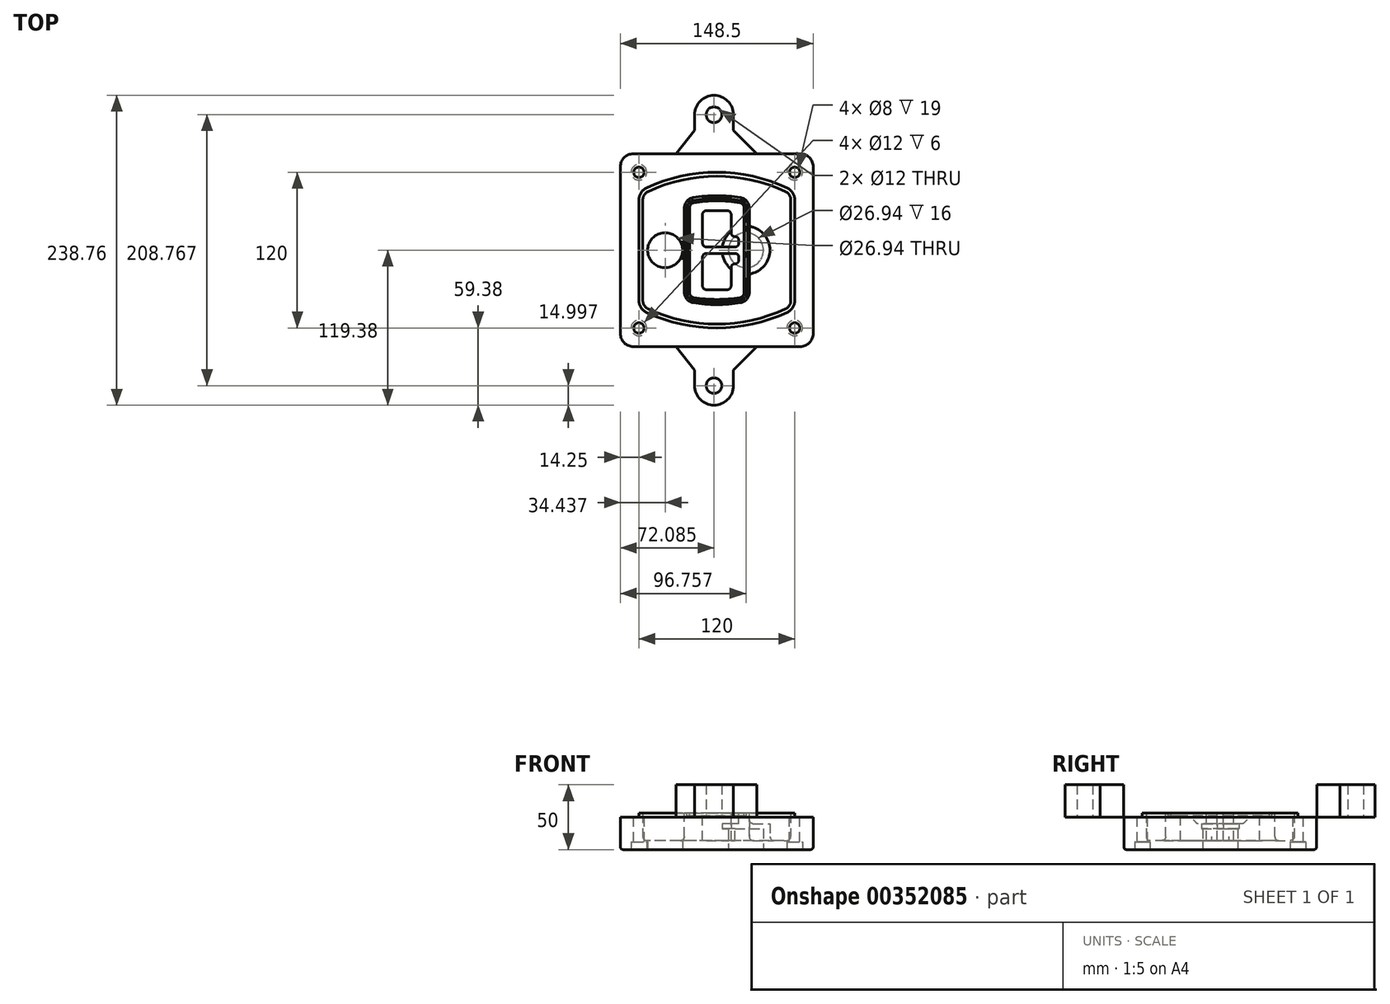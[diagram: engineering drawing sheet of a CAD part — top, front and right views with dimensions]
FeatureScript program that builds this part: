
annotation { "Feature Type Name" : "Feature", "Feature Type Description" : "" }
export const myFeature = defineFeature(function(context is Context, id is Id, definition is map)
    precondition{}
    {
        {
            var Q0;
            Q0=qCreatedBy(makeId("Top.planeOp"),FACE);
            var sketch = newSketch(context, id + "F0", { "sketchPlane" : qUnion([Q0])});
            skPoint(sketch, "E0.rect.middle", {"position": v(0, 0) * mm});
            skLineSegment(sketch, "E1.bottom", {"start": v(-64.25, -74.25) * mm, "end": v(64.25, -74.25) * mm});
            skLineSegment(sketch, "E1.top", {"start": v(-64.25, 74.25) * mm, "end": v(64.25, 74.25) * mm});
            skLineSegment(sketch, "E1.left", {"start": v(-74.25, -64.25) * mm, "end": v(-74.25, 64.25) * mm});
            skLineSegment(sketch, "E1.right", {"start": v(74.25, -64.25) * mm, "end": v(74.25, 64.25) * mm});
            skLineSegment(sketch, "E2", {"start": v(-74.25, 74.25) * mm, "end": v(74.25, -74.25) * mm, "construction": true});
            skLineSegment(sketch, "E3", {"start": v(74.25, 74.25) * mm, "end": v(-74.25, -74.25) * mm, "construction": true});
            skCircle(sketch, "E4", {"center": v(-60, 60) * mm, "radius": 4 * mm});
            skCircle(sketch, "E5", {"center": v(60, 60) * mm, "radius": 4 * mm});
            skCircle(sketch, "E6", {"center": v(60, -60) * mm, "radius": 4 * mm});
            skCircle(sketch, "E7", {"center": v(-60, -60) * mm, "radius": 4 * mm});
            skLineSegment(sketch, "E8", {"start": v(-60, 60) * mm, "end": v(60, 60) * mm, "construction": true});
            skLineSegment(sketch, "E9", {"start": v(60, 60) * mm, "end": v(60, -60) * mm, "construction": true});
            skLineSegment(sketch, "E10", {"start": v(60, -60) * mm, "end": v(-60, -60) * mm, "construction": true});
            skLineSegment(sketch, "E11", {"start": v(-60, -60) * mm, "end": v(-60, 60) * mm, "construction": true});
            skLineSegment(sketch, "E12", {"start": v(-60, 38.83) * mm, "end": v(-60, -38.83) * mm});
            skLineSegment(sketch, "E13", {"start": v(60, 38.83) * mm, "end": v(60, -38.83) * mm});
            skArc(sketch, "E14", {"start": v(54.26, 47.88) * mm, "mid": v(0, 60) * mm, "end": v(-54.26, 47.88) * mm});
            skArc(sketch, "E15", {"start": v(-54.26, -47.88) * mm, "mid": v(0, -60) * mm, "end": v(54.26, -47.88) * mm});
            skLineSegment(sketch, "E16", {"start": v(-60, 0) * mm, "end": v(60, 0) * mm, "construction": true});
            skPoint(sketch, "E17.visualSharp", {"position": v(-60, -45) * mm});
            skArc(sketch, "E17.filletArc", {"start": v(-60, -38.83) * mm, "mid": v(-58.44, -44.2) * mm, "end": v(-54.26, -47.88) * mm});
            skPoint(sketch, "E18.visualSharp", {"position": v(-60, 45) * mm});
            skArc(sketch, "E18.filletArc", {"start": v(-54.26, 47.88) * mm, "mid": v(-58.44, 44.2) * mm, "end": v(-60, 38.83) * mm});
            skPoint(sketch, "E19.visualSharp", {"position": v(60, 45) * mm});
            skArc(sketch, "E19.filletArc", {"start": v(60, 38.83) * mm, "mid": v(58.44, 44.2) * mm, "end": v(54.26, 47.88) * mm});
            skPoint(sketch, "E20.visualSharp", {"position": v(60, -45) * mm});
            skArc(sketch, "E20.filletArc", {"start": v(54.26, -47.88) * mm, "mid": v(58.44, -44.2) * mm, "end": v(60, -38.83) * mm});
            skPoint(sketch, "E21.visualSharp", {"position": v(-74.25, 74.25) * mm});
            skArc(sketch, "E21.filletArc", {"start": v(-64.25, 74.25) * mm, "mid": v(-71.32, 71.32) * mm, "end": v(-74.25, 64.25) * mm});
            skPoint(sketch, "E22.visualSharp", {"position": v(74.25, 74.25) * mm});
            skArc(sketch, "E22.filletArc", {"start": v(74.25, 64.25) * mm, "mid": v(71.32, 71.32) * mm, "end": v(64.25, 74.25) * mm});
            skPoint(sketch, "E23.visualSharp", {"position": v(74.25, -74.25) * mm});
            skArc(sketch, "E23.filletArc", {"start": v(64.25, -74.25) * mm, "mid": v(71.32, -71.32) * mm, "end": v(74.25, -64.25) * mm});
            skPoint(sketch, "E24.visualSharp", {"position": v(-74.25, -74.25) * mm});
            skArc(sketch, "E24.filletArc", {"start": v(-74.25, -64.25) * mm, "mid": v(-71.32, -71.32) * mm, "end": v(-64.25, -74.25) * mm});
            skArc(sketch, "E25.0", {"start": v(57, 38.83) * mm, "mid": v(55.9, 42.58) * mm, "end": v(52.98, 45.17) * mm});
            skLineSegment(sketch, "E25.1", {"start": v(57, 38.83) * mm, "end": v(57, -38.83) * mm});
            skArc(sketch, "E25.2", {"start": v(52.98, -45.17) * mm, "mid": v(55.9, -42.58) * mm, "end": v(57, -38.83) * mm});
            skArc(sketch, "E25.3", {"start": v(-52.98, -45.17) * mm, "mid": v(0, -57) * mm, "end": v(52.98, -45.17) * mm});
            skArc(sketch, "E25.4", {"start": v(-57, -38.83) * mm, "mid": v(-55.9, -42.58) * mm, "end": v(-52.98, -45.17) * mm});
            skArc(sketch, "E25.5", {"start": v(52.98, 45.17) * mm, "mid": v(0, 57) * mm, "end": v(-52.98, 45.17) * mm});
            skLineSegment(sketch, "E25.6", {"start": v(-57, 38.83) * mm, "end": v(-57, -38.83) * mm});
            skArc(sketch, "E25.7", {"start": v(-52.98, 45.17) * mm, "mid": v(-55.9, 42.58) * mm, "end": v(-57, 38.83) * mm});
            skArc(sketch, "E26.0", {"start": v(-55.96, 51.5) * mm, "mid": v(-61.82, 46.33) * mm, "end": v(-64, 38.83) * mm});
            skArc(sketch, "E26.1", {"start": v(55.96, 51.5) * mm, "mid": v(0, 64) * mm, "end": v(-55.96, 51.5) * mm});
            skArc(sketch, "E26.2", {"start": v(64, 38.83) * mm, "mid": v(61.82, 46.33) * mm, "end": v(55.96, 51.5) * mm});
            skLineSegment(sketch, "E26.3", {"start": v(64, 38.83) * mm, "end": v(64, -38.83) * mm});
            skArc(sketch, "E26.4", {"start": v(55.96, -51.5) * mm, "mid": v(61.82, -46.33) * mm, "end": v(64, -38.83) * mm});
            skLineSegment(sketch, "E26.5", {"start": v(-64, 38.83) * mm, "end": v(-64, -38.83) * mm});
            skArc(sketch, "E26.6", {"start": v(-55.96, -51.5) * mm, "mid": v(0, -64) * mm, "end": v(55.96, -51.5) * mm});
            skArc(sketch, "E26.7", {"start": v(-64, -38.83) * mm, "mid": v(-61.82, -46.33) * mm, "end": v(-55.96, -51.5) * mm});
            skSolve(sketch);
        }
        {
            var Q0;
            Q0=makeQuery(id+"F0.imprint","IMPRINT",FACE,{"disambiguationData":[TD([[makeQuery(id+"F0.imprint","IMPRINT",EDGE,{"derivedFrom":sQuery(id+"F0.wireOp",EDGE,"E1.bottom")}),1.0]])]});
            var Q1;
            Q1=makeQuery(id+"F0.imprint","IMPRINT",FACE,{"disambiguationData":[TD([[makeQuery(id+"F0.imprint","IMPRINT",EDGE,{"derivedFrom":sQuery(id+"F0.wireOp",EDGE,"E12")}),1.0]])]});
            var Q2;
            Q2=makeQuery(id+"F0.imprint","IMPRINT",FACE,{"disambiguationData":[TD([[makeQuery(id+"F0.imprint","IMPRINT",EDGE,{"derivedFrom":sQuery(id+"F0.wireOp",EDGE,"E25.0")}),1.0]])]});
            var Q3;
            Q3=makeQuery(id+"F0.imprint","IMPRINT",FACE,{"disambiguationData":[TD([[makeQuery(id+"F0.imprint","IMPRINT",EDGE,{"derivedFrom":sQuery(id+"F0.wireOp",EDGE,"E12")}),-1.0]])]});
            extrude(context, id + "F1", {"entities" : qUnion([Q0, Q1, Q2, Q3]), "oppositeDirection" : true, "depth" : 25 * mm});
        }
        {
            var Q0;
            Q0=makeQuery(id+"F0.imprint","IMPRINT",FACE,{"disambiguationData":[TD([[makeQuery(id+"F0.imprint","IMPRINT",EDGE,{"derivedFrom":sQuery(id+"F0.wireOp",EDGE,"E12")}),1.0]])]});
            extrude(context, id + "F2", {"entities" : qUnion([Q0]), "operationType" : NewBodyOperationType.ADD, "depth" : 3 * mm});
        }
        {
            var Q0;
            Q0=makeQuery(id+"F0.imprint","IMPRINT",FACE,{"disambiguationData":[TD([[makeQuery(id+"F0.imprint","IMPRINT",EDGE,{"derivedFrom":sQuery(id+"F0.wireOp",EDGE,"E25.0")}),1.0]])]});
            extrude(context, id + "F3", {"entities" : qUnion([Q0]), "operationType" : NewBodyOperationType.REMOVE, "oppositeDirection" : true, "depth" : 18 * mm});
        }
        {
            var Q0;
            Q0=makeQuery(id+"F2.opExtrude","CAP_FACE",FACE,{"disambiguationData":[OSD([sQuery(id+"F0.wireOp",EDGE,"E12"),sQuery(id+"F0.wireOp",EDGE,"E13"),sQuery(id+"F0.wireOp",EDGE,"E14"),sQuery(id+"F0.wireOp",EDGE,"E15"),sQuery(id+"F0.wireOp",EDGE,"E17.filletArc"),sQuery(id+"F0.wireOp",EDGE,"E18.filletArc"),sQuery(id+"F0.wireOp",EDGE,"E19.filletArc"),sQuery(id+"F0.wireOp",EDGE,"E20.filletArc"),sQuery(id+"F0.wireOp",EDGE,"E25.0"),sQuery(id+"F0.wireOp",EDGE,"E25.1"),sQuery(id+"F0.wireOp",EDGE,"E25.2"),sQuery(id+"F0.wireOp",EDGE,"E25.3"),sQuery(id+"F0.wireOp",EDGE,"E25.4"),sQuery(id+"F0.wireOp",EDGE,"E25.5"),sQuery(id+"F0.wireOp",EDGE,"E25.6"),sQuery(id+"F0.wireOp",EDGE,"E25.7")])],"isStart":false});
            var sketch = newSketch(context, id + "F4", { "sketchPlane" : qUnion([Q0])});
            skArc(sketch, "E27.0", {"start": v(-18.34, -40.45) * mm, "mid": v(0, -42) * mm, "end": v(18.34, -40.45) * mm});
            skArc(sketch, "E28.0", {"start": v(18.34, 40.45) * mm, "mid": v(0, 42) * mm, "end": v(-18.34, 40.45) * mm});
            skLineSegment(sketch, "E29", {"start": v(-25, 32.57) * mm, "end": v(-25, -32.57) * mm});
            skLineSegment(sketch, "E30", {"start": v(25, 32.57) * mm, "end": v(25, -32.57) * mm});
            skLineSegment(sketch, "E31", {"start": v(-25, 39.1) * mm, "end": v(25, 39.1) * mm, "construction": true});
            skLineSegment(sketch, "E32", {"start": v(-25, -39.1) * mm, "end": v(25, -39.1) * mm, "construction": true});
            skPoint(sketch, "E33.visualSharp", {"position": v(-25, 39.1) * mm});
            skArc(sketch, "E33.filletArc", {"start": v(-18.34, 40.45) * mm, "mid": v(-23.11, 37.73) * mm, "end": v(-25, 32.57) * mm});
            skPoint(sketch, "E34.visualSharp", {"position": v(25, 39.1) * mm});
            skArc(sketch, "E34.filletArc", {"start": v(25, 32.57) * mm, "mid": v(23.11, 37.73) * mm, "end": v(18.34, 40.45) * mm});
            skPoint(sketch, "E35.visualSharp", {"position": v(25, -39.1) * mm});
            skArc(sketch, "E35.filletArc", {"start": v(18.34, -40.45) * mm, "mid": v(23.11, -37.73) * mm, "end": v(25, -32.57) * mm});
            skPoint(sketch, "E36.visualSharp", {"position": v(-25, -39.1) * mm});
            skArc(sketch, "E36.filletArc", {"start": v(-25, -32.57) * mm, "mid": v(-23.11, -37.73) * mm, "end": v(-18.34, -40.45) * mm});
            skArc(sketch, "E37.0", {"start": v(52.98, 45.17) * mm, "mid": v(0, 57) * mm, "end": v(-52.98, 45.17) * mm});
            skArc(sketch, "E37.1", {"start": v(-52.98, 45.17) * mm, "mid": v(-55.9, 42.58) * mm, "end": v(-57, 38.83) * mm});
            skLineSegment(sketch, "E37.2", {"start": v(-57, 38.83) * mm, "end": v(-57, -38.83) * mm});
            skArc(sketch, "E37.3", {"start": v(-57, -38.83) * mm, "mid": v(-55.9, -42.58) * mm, "end": v(-52.98, -45.17) * mm});
            skArc(sketch, "E37.4", {"start": v(-52.98, -45.17) * mm, "mid": v(0, -57) * mm, "end": v(52.98, -45.17) * mm});
            skArc(sketch, "E37.5", {"start": v(52.98, -45.17) * mm, "mid": v(55.9, -42.58) * mm, "end": v(57, -38.83) * mm});
            skLineSegment(sketch, "E37.6", {"start": v(57, 38.83) * mm, "end": v(57, -38.83) * mm});
            skArc(sketch, "E37.7", {"start": v(57, 38.83) * mm, "mid": v(55.9, 42.58) * mm, "end": v(52.98, 45.17) * mm});
            skLineSegment(sketch, "E38.0", {"start": v(23, 32.57) * mm, "end": v(23, -32.57) * mm});
            skArc(sketch, "E38.1", {"start": v(18, -38.48) * mm, "mid": v(21.58, -36.44) * mm, "end": v(23, -32.57) * mm});
            skArc(sketch, "E38.2", {"start": v(-18, -38.48) * mm, "mid": v(0, -40) * mm, "end": v(18, -38.48) * mm});
            skArc(sketch, "E38.3", {"start": v(-23, -32.57) * mm, "mid": v(-21.58, -36.44) * mm, "end": v(-18, -38.48) * mm});
            skLineSegment(sketch, "E38.4", {"start": v(-23, 32.57) * mm, "end": v(-23, -32.57) * mm});
            skArc(sketch, "E38.5", {"start": v(23, 32.57) * mm, "mid": v(21.58, 36.44) * mm, "end": v(18, 38.48) * mm});
            skArc(sketch, "E38.6", {"start": v(-18, 38.48) * mm, "mid": v(-21.58, 36.44) * mm, "end": v(-23, 32.57) * mm});
            skArc(sketch, "E38.7", {"start": v(18, 38.48) * mm, "mid": v(0, 40) * mm, "end": v(-18, 38.48) * mm});
            skArc(sketch, "E39.0", {"start": v(21, 32.57) * mm, "mid": v(20.06, 35.15) * mm, "end": v(17.67, 36.5) * mm});
            skLineSegment(sketch, "E39.1", {"start": v(21, 32.57) * mm, "end": v(21, -32.57) * mm});
            skArc(sketch, "E39.2", {"start": v(17.67, -36.5) * mm, "mid": v(20.06, -35.15) * mm, "end": v(21, -32.57) * mm});
            skArc(sketch, "E39.3", {"start": v(-17.67, -36.5) * mm, "mid": v(0, -38) * mm, "end": v(17.67, -36.5) * mm});
            skArc(sketch, "E39.4", {"start": v(-21, -32.57) * mm, "mid": v(-20.06, -35.15) * mm, "end": v(-17.67, -36.5) * mm});
            skArc(sketch, "E39.5", {"start": v(17.67, 36.5) * mm, "mid": v(0, 38) * mm, "end": v(-17.67, 36.5) * mm});
            skLineSegment(sketch, "E39.6", {"start": v(-21, 32.57) * mm, "end": v(-21, -32.57) * mm});
            skArc(sketch, "E39.7", {"start": v(-17.67, 36.5) * mm, "mid": v(-20.06, 35.15) * mm, "end": v(-21, 32.57) * mm});
            skLineSegment(sketch, "E40", {"start": v(-25, 0) * mm, "end": v(25, 0) * mm, "construction": true});
            skLineSegment(sketch, "E41", {"start": v(-11, 5.5) * mm, "end": v(-11, 27.5) * mm});
            skLineSegment(sketch, "E42", {"start": v(-8, 30.5) * mm, "end": v(8, 30.5) * mm});
            skLineSegment(sketch, "E43", {"start": v(11, 27.5) * mm, "end": v(11, 13.5) * mm});
            skLineSegment(sketch, "E44", {"start": v(14, 10.5) * mm, "end": v(14, 10.5) * mm});
            skLineSegment(sketch, "E45", {"start": v(17, 7.5) * mm, "end": v(17, 5.5) * mm});
            skLineSegment(sketch, "E46", {"start": v(14, 2.5) * mm, "end": v(-8, 2.5) * mm});
            skPoint(sketch, "E47.visualSharp", {"position": v(-11, 30.5) * mm});
            skArc(sketch, "E47.filletArc", {"start": v(-8, 30.5) * mm, "mid": v(-10.12, 29.62) * mm, "end": v(-11, 27.5) * mm});
            skPoint(sketch, "E48.visualSharp", {"position": v(11, 30.5) * mm});
            skArc(sketch, "E48.filletArc", {"start": v(11, 27.5) * mm, "mid": v(10.12, 29.62) * mm, "end": v(8, 30.5) * mm});
            skPoint(sketch, "E49.visualSharp", {"position": v(11, 10.5) * mm});
            skArc(sketch, "E49.filletArc", {"start": v(11, 13.5) * mm, "mid": v(11.88, 11.38) * mm, "end": v(14, 10.5) * mm});
            skPoint(sketch, "E50.visualSharp", {"position": v(17, 10.5) * mm});
            skArc(sketch, "E50.filletArc", {"start": v(17, 7.5) * mm, "mid": v(16.12, 9.62) * mm, "end": v(14, 10.5) * mm});
            skPoint(sketch, "E51.visualSharp", {"position": v(17, 2.5) * mm});
            skArc(sketch, "E51.filletArc", {"start": v(14, 2.5) * mm, "mid": v(16.12, 3.38) * mm, "end": v(17, 5.5) * mm});
            skPoint(sketch, "E52.visualSharp", {"position": v(-11, 2.5) * mm});
            skArc(sketch, "E52.filletArc", {"start": v(-11, 5.5) * mm, "mid": v(-10.12, 3.38) * mm, "end": v(-8, 2.5) * mm});
            skLineSegment(sketch, "E53.0.MirrorCS", {"start": v(14, -2.5) * mm, "end": v(-8, -2.5) * mm});
            skArc(sketch, "E54.0.MirrorCS", {"start": v(-11, -5.5) * mm, "mid": v(-10.12, -3.38) * mm, "end": v(-8, -2.5) * mm});
            skLineSegment(sketch, "E55.0.MirrorCS", {"start": v(-11, -5.5) * mm, "end": v(-11, -27.5) * mm});
            skArc(sketch, "E56.0.MirrorCS", {"start": v(-8, -30.5) * mm, "mid": v(-10.12, -29.62) * mm, "end": v(-11, -27.5) * mm});
            skLineSegment(sketch, "E57.0.MirrorCS", {"start": v(-8, -30.5) * mm, "end": v(8, -30.5) * mm});
            skArc(sketch, "E58.0.MirrorCS", {"start": v(11, -27.5) * mm, "mid": v(10.12, -29.62) * mm, "end": v(8, -30.5) * mm});
            skLineSegment(sketch, "E59.0.MirrorCS", {"start": v(11, -27.5) * mm, "end": v(11, -13.5) * mm});
            skArc(sketch, "E60.0.MirrorCS", {"start": v(11, -13.5) * mm, "mid": v(11.88, -11.38) * mm, "end": v(14, -10.5) * mm});
            skArc(sketch, "E61.0.MirrorCS", {"start": v(17, -7.5) * mm, "mid": v(16.12, -9.62) * mm, "end": v(14, -10.5) * mm});
            skLineSegment(sketch, "E62.0.MirrorCS", {"start": v(17, -7.5) * mm, "end": v(17, -5.5) * mm});
            skArc(sketch, "E63.0.MirrorCS", {"start": v(14, -2.5) * mm, "mid": v(16.12, -3.38) * mm, "end": v(17, -5.5) * mm});
            skSolve(sketch);
        }
        {
            var Q0;
            Q0=makeQuery(id+"F4.imprint","IMPRINT",FACE,{"disambiguationData":[TD([[makeQuery(id+"F4.imprint","IMPRINT",EDGE,{"derivedFrom":sQuery(id+"F4.wireOp",EDGE,"E27.0")}),1.0]])]});
            var Q1;
            Q1=makeQuery(id+"F4.imprint","IMPRINT",FACE,{"disambiguationData":[TD([[makeQuery(id+"F4.imprint","IMPRINT",EDGE,{"derivedFrom":sQuery(id+"F4.wireOp",EDGE,"E38.0")}),-1.0]])]});
            var Q2;
            Q2=makeQuery(id+"F4.imprint","IMPRINT",FACE,{"disambiguationData":[TD([[makeQuery(id+"F4.imprint","IMPRINT",EDGE,{"derivedFrom":sQuery(id+"F4.wireOp",EDGE,"E39.0")}),1.0]])]});
            extrude(context, id + "F5", {"entities" : qUnion([Q0, Q1, Q2]), "operationType" : NewBodyOperationType.ADD, "endBound" : BoundingType.UP_TO_NEXT, "oppositeDirection" : true, "depth" : 25 * mm});
        }
        {
            var Q0;
            Q0=makeQuery(id+"F4.imprint","IMPRINT",FACE,{"disambiguationData":[TD([[makeQuery(id+"F4.imprint","IMPRINT",EDGE,{"derivedFrom":sQuery(id+"F4.wireOp",EDGE,"E38.0")}),-1.0]])]});
            extrude(context, id + "F6", {"entities" : qUnion([Q0]), "operationType" : NewBodyOperationType.REMOVE, "oppositeDirection" : true, "depth" : 2 * mm});
        }
        {
            var Q0;
            Q0=makeQuery(id+"F1.opExtrude","CAP_FACE",FACE,{"disambiguationData":[OSD([sQuery(id+"F0.wireOp",EDGE,"E1.bottom"),sQuery(id+"F0.wireOp",EDGE,"E1.top"),sQuery(id+"F0.wireOp",EDGE,"E1.left"),sQuery(id+"F0.wireOp",EDGE,"E1.right"),sQuery(id+"F0.wireOp",EDGE,"E4"),sQuery(id+"F0.wireOp",EDGE,"E5"),sQuery(id+"F0.wireOp",EDGE,"E6"),sQuery(id+"F0.wireOp",EDGE,"E7"),sQuery(id+"F0.wireOp",EDGE,"E21.filletArc"),sQuery(id+"F0.wireOp",EDGE,"E22.filletArc"),sQuery(id+"F0.wireOp",EDGE,"E23.filletArc"),sQuery(id+"F0.wireOp",EDGE,"E24.filletArc")])],"isStart":false});
            var sketch = newSketch(context, id + "F7", { "sketchPlane" : qUnion([Q0])});
            skCircle(sketch, "E64", {"center": v(22.5, 0) * mm, "radius": 13.47 * mm});
            skCircle(sketch, "E65", {"center": v(-39.81, 0) * mm, "radius": 13.47 * mm});
            skLineSegment(sketch, "E66", {"start": v(74.25, 0) * mm, "end": v(-74.25, 0) * mm});
            skCircle(sketch, "E67", {"center": v(22.5, 0) * mm, "radius": 18.47 * mm});
            skCircle(sketch, "E68", {"center": v(60, -60) * mm, "radius": 6 * mm});
            skCircle(sketch, "E69", {"center": v(-60, -60) * mm, "radius": 6 * mm});
            skCircle(sketch, "E70", {"center": v(-60, 60) * mm, "radius": 6 * mm});
            skCircle(sketch, "E71", {"center": v(60, 60) * mm, "radius": 6 * mm});
            skSolve(sketch);
        }
        {
            var Q0;
            {var subQ1=sQuery(id+"F7.wireOp",EDGE,"E66");var subQ4=sQuery(id+"F7.wireOp",EDGE,"E64");var subQ6=makeQuery(id+"F7.imprint","INTERSECT",VERTEX,{"disambiguationData":[OD(0.0)],"derivedFrom":[subQ4,subQ1]});Q0=makeQuery(id+"F7.imprint","IMPRINT",FACE,{"disambiguationData":[TD([[makeQuery(id+"F7.imprint","IMPRINT",EDGE,{"disambiguationData":[TD([[subQ6,-1.0]])],"derivedFrom":subQ4}),-1.0]])]});}
            var Q1;
            {var subQ0=sQuery(id+"F7.wireOp",EDGE,"E66");var subQ1=sQuery(id+"F7.wireOp",EDGE,"E64");var subQ3=makeQuery(id+"F7.imprint","INTERSECT",VERTEX,{"disambiguationData":[OD(0.0)],"derivedFrom":[subQ1,subQ0]});Q1=makeQuery(id+"F7.imprint","IMPRINT",FACE,{"disambiguationData":[TD([[makeQuery(id+"F7.imprint","IMPRINT",EDGE,{"disambiguationData":[TD([[subQ3,-1.0]])],"derivedFrom":subQ1}),1.0]])]});}
            var Q2;
            {var subQ0=sQuery(id+"F7.wireOp",EDGE,"E66");var subQ1=sQuery(id+"F7.wireOp",EDGE,"E64");var subQ3=makeQuery(id+"F7.imprint","INTERSECT",VERTEX,{"disambiguationData":[OD(0.0)],"derivedFrom":[subQ1,subQ0]});Q2=makeQuery(id+"F7.imprint","IMPRINT",FACE,{"disambiguationData":[TD([[makeQuery(id+"F7.imprint","IMPRINT",EDGE,{"disambiguationData":[TD([[subQ3,1.0]])],"derivedFrom":subQ1}),1.0]])]});}
            var Q3;
            {var subQ1=sQuery(id+"F7.wireOp",EDGE,"E66");var subQ4=sQuery(id+"F7.wireOp",EDGE,"E64");var subQ6=makeQuery(id+"F7.imprint","INTERSECT",VERTEX,{"disambiguationData":[OD(0.0)],"derivedFrom":[subQ4,subQ1]});Q3=makeQuery(id+"F7.imprint","IMPRINT",FACE,{"disambiguationData":[TD([[makeQuery(id+"F7.imprint","IMPRINT",EDGE,{"disambiguationData":[TD([[subQ6,1.0]])],"derivedFrom":subQ4}),-1.0]])]});}
            extrude(context, id + "F8", {"entities" : qUnion([Q0, Q1, Q2, Q3]), "operationType" : NewBodyOperationType.ADD, "oppositeDirection" : true, "depth" : 20 * mm});
        }
        {
            var Q0;
            {var subQ0=sQuery(id+"F7.wireOp",EDGE,"E66");var subQ1=sQuery(id+"F7.wireOp",EDGE,"E64");var subQ3=makeQuery(id+"F7.imprint","INTERSECT",VERTEX,{"disambiguationData":[OD(0.0)],"derivedFrom":[subQ1,subQ0]});Q0=makeQuery(id+"F7.imprint","IMPRINT",FACE,{"disambiguationData":[TD([[makeQuery(id+"F7.imprint","IMPRINT",EDGE,{"disambiguationData":[TD([[subQ3,-1.0]])],"derivedFrom":subQ1}),1.0]])]});}
            var Q1;
            {var subQ0=sQuery(id+"F7.wireOp",EDGE,"E66");var subQ1=sQuery(id+"F7.wireOp",EDGE,"E64");var subQ3=makeQuery(id+"F7.imprint","INTERSECT",VERTEX,{"disambiguationData":[OD(0.0)],"derivedFrom":[subQ1,subQ0]});Q1=makeQuery(id+"F7.imprint","IMPRINT",FACE,{"disambiguationData":[TD([[makeQuery(id+"F7.imprint","IMPRINT",EDGE,{"disambiguationData":[TD([[subQ3,1.0]])],"derivedFrom":subQ1}),1.0]])]});}
            extrude(context, id + "F9", {"entities" : qUnion([Q0, Q1]), "operationType" : NewBodyOperationType.REMOVE, "oppositeDirection" : true, "depth" : 16 * mm});
        }
        {
            var Q0;
            {var subQ0=sQuery(id+"F7.wireOp",EDGE,"E66");var subQ1=sQuery(id+"F7.wireOp",EDGE,"E65");var subQ3=makeQuery(id+"F7.imprint","INTERSECT",VERTEX,{"disambiguationData":[OD(0.0)],"derivedFrom":[subQ1,subQ0]});Q0=makeQuery(id+"F7.imprint","IMPRINT",FACE,{"disambiguationData":[TD([[makeQuery(id+"F7.imprint","IMPRINT",EDGE,{"disambiguationData":[TD([[subQ3,-1.0]])],"derivedFrom":subQ1}),1.0]])]});}
            var Q1;
            {var subQ0=sQuery(id+"F7.wireOp",EDGE,"E66");var subQ1=sQuery(id+"F7.wireOp",EDGE,"E65");var subQ3=makeQuery(id+"F7.imprint","INTERSECT",VERTEX,{"disambiguationData":[OD(0.0)],"derivedFrom":[subQ1,subQ0]});Q1=makeQuery(id+"F7.imprint","IMPRINT",FACE,{"disambiguationData":[TD([[makeQuery(id+"F7.imprint","IMPRINT",EDGE,{"disambiguationData":[TD([[subQ3,1.0]])],"derivedFrom":subQ1}),1.0]])]});}
            extrude(context, id + "F10", {"entities" : qUnion([Q0, Q1]), "operationType" : NewBodyOperationType.REMOVE, "oppositeDirection" : true, "depth" : 25 * mm});
        }
        {
            var Q0;
            Q0=makeQuery(id+"F7.imprint","IMPRINT",FACE,{"disambiguationData":[TD([[makeQuery(id+"F7.imprint","IMPRINT",EDGE,{"derivedFrom":sQuery(id+"F7.wireOp",EDGE,"E68")}),1.0]])]});
            var Q1;
            Q1=makeQuery(id+"F7.imprint","IMPRINT",FACE,{"disambiguationData":[TD([[makeQuery(id+"F7.imprint","IMPRINT",EDGE,{"derivedFrom":makeQuery(id+"F1.opExtrude","CAP_EDGE",EDGE,{"disambiguationData":[OSD([sQuery(id+"F0.wireOp",EDGE,"E5")])],"isStart":false})}),-1.0]])]});
            var Q2;
            Q2=makeQuery(id+"F7.imprint","IMPRINT",FACE,{"disambiguationData":[TD([[makeQuery(id+"F7.imprint","IMPRINT",EDGE,{"derivedFrom":sQuery(id+"F7.wireOp",EDGE,"E69")}),1.0]])]});
            var Q3;
            Q3=makeQuery(id+"F7.imprint","IMPRINT",FACE,{"disambiguationData":[TD([[makeQuery(id+"F7.imprint","IMPRINT",EDGE,{"derivedFrom":makeQuery(id+"F1.opExtrude","CAP_EDGE",EDGE,{"disambiguationData":[OSD([sQuery(id+"F0.wireOp",EDGE,"E4")])],"isStart":false})}),-1.0]])]});
            var Q4;
            Q4=makeQuery(id+"F7.imprint","IMPRINT",FACE,{"disambiguationData":[TD([[makeQuery(id+"F7.imprint","IMPRINT",EDGE,{"derivedFrom":sQuery(id+"F7.wireOp",EDGE,"E70")}),1.0]])]});
            var Q5;
            Q5=makeQuery(id+"F7.imprint","IMPRINT",FACE,{"disambiguationData":[TD([[makeQuery(id+"F7.imprint","IMPRINT",EDGE,{"derivedFrom":makeQuery(id+"F1.opExtrude","CAP_EDGE",EDGE,{"disambiguationData":[OSD([sQuery(id+"F0.wireOp",EDGE,"E7")])],"isStart":false})}),-1.0]])]});
            var Q6;
            Q6=makeQuery(id+"F7.imprint","IMPRINT",FACE,{"disambiguationData":[TD([[makeQuery(id+"F7.imprint","IMPRINT",EDGE,{"derivedFrom":sQuery(id+"F7.wireOp",EDGE,"E71")}),1.0]])]});
            var Q7;
            Q7=makeQuery(id+"F7.imprint","IMPRINT",FACE,{"disambiguationData":[TD([[makeQuery(id+"F7.imprint","IMPRINT",EDGE,{"derivedFrom":makeQuery(id+"F1.opExtrude","CAP_EDGE",EDGE,{"disambiguationData":[OSD([sQuery(id+"F0.wireOp",EDGE,"E6")])],"isStart":false})}),-1.0]])]});
            extrude(context, id + "F11", {"entities" : qUnion([Q0, Q1, Q2, Q3, Q4, Q5, Q6, Q7]), "operationType" : NewBodyOperationType.REMOVE, "oppositeDirection" : true, "depth" : 6 * mm});
        }
        {
            var Q0;
            Q0=makeQuery(id+"F9.boolean.opBoolean","COPY",FACE,{"derivedFrom":makeQuery(id+"F9.opExtrude","CAP_FACE",FACE,{"disambiguationData":[OSD([sQuery(id+"F7.wireOp",EDGE,"E64")])],"isStart":false})});
            var sketch = newSketch(context, id + "F12", { "sketchPlane" : qUnion([Q0])});
            skArc(sketch, "E72.0", {"start": v(11, 14.45) * mm, "mid": v(6.45, 9.13) * mm, "end": v(4.2, 2.5) * mm});
            skArc(sketch, "E72.1", {"start": v(4.2, -2.5) * mm, "mid": v(6.45, -9.13) * mm, "end": v(11, -14.45) * mm});
            skLineSegment(sketch, "E73", {"start": v(4.2, -2.5) * mm, "end": v(14, -2.5) * mm});
            skLineSegment(sketch, "E74.0", {"start": v(14, 2.5) * mm, "end": v(4.2, 2.5) * mm});
            skArc(sketch, "E74.1", {"start": v(14, 2.5) * mm, "mid": v(16.12, 3.38) * mm, "end": v(17, 5.5) * mm});
            skLineSegment(sketch, "E74.2", {"start": v(17, 7.5) * mm, "end": v(17, 5.5) * mm});
            skArc(sketch, "E74.3", {"start": v(17, 7.5) * mm, "mid": v(16.12, 9.62) * mm, "end": v(14, 10.5) * mm});
            skArc(sketch, "E74.4", {"start": v(11, 13.5) * mm, "mid": v(11.88, 11.38) * mm, "end": v(14, 10.5) * mm});
            skLineSegment(sketch, "E74.5", {"start": v(11, 14.45) * mm, "end": v(11, 13.5) * mm});
            skLineSegment(sketch, "E74.7", {"start": v(14, -2.5) * mm, "end": v(4.2, -2.5) * mm});
            skArc(sketch, "E74.8", {"start": v(14, -2.5) * mm, "mid": v(16.12, -3.38) * mm, "end": v(17, -5.5) * mm});
            skLineSegment(sketch, "E74.9", {"start": v(17, -7.5) * mm, "end": v(17, -5.5) * mm});
            skArc(sketch, "E74.10", {"start": v(17, -7.5) * mm, "mid": v(16.12, -9.62) * mm, "end": v(14, -10.5) * mm});
            skArc(sketch, "E74.11", {"start": v(11, -13.5) * mm, "mid": v(11.88, -11.38) * mm, "end": v(14, -10.5) * mm});
            skLineSegment(sketch, "E74.12", {"start": v(11, -14.45) * mm, "end": v(11, -13.5) * mm});
            skPoint(sketch, "E75.orphan", {"position": v(11, -27.5) * mm});
            skPoint(sketch, "E76.orphan", {"position": v(-8, -2.5) * mm});
            skPoint(sketch, "E77.orphan", {"position": v(-8, 2.5) * mm});
            skPoint(sketch, "E78.orphan", {"position": v(11, 27.5) * mm});
            skSolve(sketch);
        }
        {
            var Q0;
            {var subQ7=sQuery(id+"F12.wireOp",EDGE,"E72.0");var subQ14=sQuery(id+"F12.wireOp",EDGE,"E72.1");var subQ16=sQuery(id+"F12.wireOp",EDGE,"E74.1");var subQ18=sQuery(id+"F12.wireOp",EDGE,"E74.8");Q0=qUnion([makeQuery(id+"F12.imprint","IMPRINT",FACE,{"disambiguationData":[TD([[makeQuery(id+"F12.imprint","IMPRINT",EDGE,{"derivedFrom":subQ7}),1.0]])]}),makeQuery(id+"F12.imprint","IMPRINT",FACE,{"disambiguationData":[TD([[makeQuery(id+"F12.imprint","IMPRINT",EDGE,{"derivedFrom":subQ14}),1.0]])]}),makeQuery(id+"F12.imprint","IMPRINT",FACE,{"disambiguationData":[TD([[makeQuery(id+"F12.imprint","IMPRINT",EDGE,{"derivedFrom":subQ16}),1.0]])]}),makeQuery(id+"F12.imprint","IMPRINT",FACE,{"disambiguationData":[TD([[makeQuery(id+"F12.imprint","IMPRINT",EDGE,{"derivedFrom":subQ18}),-1.0]])]})]);}
            var Q1;
            Q1=makeQuery(id+"F5.boolean.opBoolean","SPLIT",FACE,{"disambiguationData":[TD([makeQuery(id+"F5.opExtrude","SWEPT_FACE",FACE,{"disambiguationData":[OSD([sQuery(id+"F4.wireOp",EDGE,"E41")])]})])],"derivedFrom":makeQuery(id+"F3.boolean.opBoolean","COPY",FACE,{"derivedFrom":makeQuery(id+"F3.opExtrude","CAP_FACE",FACE,{"disambiguationData":[OSD([sQuery(id+"F0.wireOp",EDGE,"E25.0"),sQuery(id+"F0.wireOp",EDGE,"E25.1"),sQuery(id+"F0.wireOp",EDGE,"E25.2"),sQuery(id+"F0.wireOp",EDGE,"E25.3"),sQuery(id+"F0.wireOp",EDGE,"E25.4"),sQuery(id+"F0.wireOp",EDGE,"E25.5"),sQuery(id+"F0.wireOp",EDGE,"E25.6"),sQuery(id+"F0.wireOp",EDGE,"E25.7")])],"isStart":false})})});
            extrude(context, id + "F13", {"entities" : qUnion([Q0]), "operationType" : NewBodyOperationType.REMOVE, "endBound" : BoundingType.UP_TO_SURFACE, "endBoundEntityFace" : qUnion([Q1]), "depth" : 25 * mm});
        }
        {
            var Q0;
            Q0=makeQuery(id+"F3.boolean.opBoolean","COPY",EDGE,{"derivedFrom":makeQuery(id+"F3.opExtrude","CAP_EDGE",EDGE,{"disambiguationData":[OSD([sQuery(id+"F0.wireOp",EDGE,"E25.6")])],"isStart":false})});
            var Q1;
            Q1=makeQuery(id+"F8.boolean.opBoolean","INTERSECT",EDGE,{"derivedFrom":[makeQuery(id+"F5.opExtrude","SWEPT_FACE",FACE,{"disambiguationData":[OSD([sQuery(id+"F4.wireOp",EDGE,"E30")])]}),makeQuery(id+"F8.opExtrude","CAP_FACE",FACE,{"disambiguationData":[OSD([sQuery(id+"F7.wireOp",EDGE,"E67")])],"isStart":false})]});
            var Q2;
            Q2=makeQuery(id+"F8.boolean.opBoolean","INTERSECT",EDGE,{"disambiguationData":[OD(1.0)],"derivedFrom":[makeQuery(id+"F5.opExtrude","SWEPT_FACE",FACE,{"disambiguationData":[OSD([sQuery(id+"F4.wireOp",EDGE,"E30")])]}),makeQuery(id+"F8.opExtrude","SWEPT_FACE",FACE,{"disambiguationData":[OSD([sQuery(id+"F7.wireOp",EDGE,"E67")])]})]});
            var Q3;
            {var subQ0=sQuery(id+"F4.wireOp",EDGE,"E30");Q3=makeQuery(id+"F8.boolean.opBoolean","SPLIT",EDGE,{"disambiguationData":[TD([makeQuery(id+"F5.opExtrude","SWEPT_FACE",FACE,{"disambiguationData":[OSD([sQuery(id+"F4.wireOp",EDGE,"E35.filletArc")])]})])],"derivedFrom":makeQuery(id+"F5.opExtrude","CAP_EDGE",EDGE,{"disambiguationData":[OSD([subQ0])],"isStart":false})});}
            var Q4;
            {var subQ0=sQuery(id+"F0.wireOp",EDGE,"E25.7");var subQ1=sQuery(id+"F0.wireOp",EDGE,"E25.1");var subQ2=sQuery(id+"F0.wireOp",EDGE,"E25.6");var subQ3=sQuery(id+"F0.wireOp",EDGE,"E25.5");var subQ4=sQuery(id+"F0.wireOp",EDGE,"E25.4");var subQ5=sQuery(id+"F0.wireOp",EDGE,"E25.0");var subQ6=sQuery(id+"F0.wireOp",EDGE,"E25.2");var subQ7=sQuery(id+"F0.wireOp",EDGE,"E25.3");Q4=makeQuery(id+"F8.boolean.opBoolean","INTERSECT",EDGE,{"derivedFrom":[makeQuery(id+"F5.boolean.opBoolean","SPLIT",FACE,{"disambiguationData":[TD([makeQuery(id+"F2.opExtrude","SWEPT_FACE",FACE,{"disambiguationData":[OSD([subQ5])]})])],"derivedFrom":makeQuery(id+"F3.boolean.opBoolean","COPY",FACE,{"derivedFrom":makeQuery(id+"F3.opExtrude","CAP_FACE",FACE,{"disambiguationData":[OSD([subQ5,subQ1,subQ6,subQ7,subQ4,subQ3,subQ2,subQ0])],"isStart":false})})}),makeQuery(id+"F8.opExtrude","SWEPT_FACE",FACE,{"disambiguationData":[OSD([sQuery(id+"F7.wireOp",EDGE,"E67")])]})]});}
            var Q5;
            Q5=makeQuery(id+"F8.boolean.opBoolean","INTERSECT",EDGE,{"disambiguationData":[OD(0.0)],"derivedFrom":[makeQuery(id+"F5.opExtrude","SWEPT_FACE",FACE,{"disambiguationData":[OSD([sQuery(id+"F4.wireOp",EDGE,"E30")])]}),makeQuery(id+"F8.opExtrude","SWEPT_FACE",FACE,{"disambiguationData":[OSD([sQuery(id+"F7.wireOp",EDGE,"E67")])]})]});
            fillet(context, id + "F14", {"entities" : qUnion([Q0, Q1, Q2, Q3, Q4, Q5]), "radius" : 3 * mm, "tangentPropagation" : true, "allowEdgeOverflow" : false});
        }
        {
            var Q0;
            Q0=makeQuery(id+"F1.opExtrude","CAP_EDGE",EDGE,{"disambiguationData":[OSD([sQuery(id+"F0.wireOp",EDGE,"E1.bottom")])],"isStart":false});
            fillet(context, id + "F15", {"entities" : qUnion([Q0]), "radius" : 2 * mm, "tangentPropagation" : true, "allowEdgeOverflow" : false});
        }
        {
            var Q0;
            Q0=qCreatedBy(makeId("Top.planeOp"),FACE);
            var sketch = newSketch(context, id + "F16", { "sketchPlane" : qUnion([Q0])});
            skLineSegment(sketch, "E79", {"start": v(-31.53, 74.38) * mm, "end": v(-17.16, 92.38) * mm});
            skLineSegment(sketch, "E80", {"start": v(-17.16, 92.38) * mm, "end": v(-17.16, 104.38) * mm});
            skLineSegment(sketch, "E81", {"start": v(-31.53, 74.38) * mm, "end": v(30.84, 74.38) * mm});
            skLineSegment(sketch, "E82", {"start": v(30.84, 74.38) * mm, "end": v(12.84, 92.38) * mm});
            skLineSegment(sketch, "E83", {"start": v(12.84, 92.38) * mm, "end": v(12.84, 104.38) * mm});
            skArc(sketch, "E84", {"start": v(12.84, 104.38) * mm, "mid": v(-2.16, 119.38) * mm, "end": v(-17.16, 104.38) * mm});
            skCircle(sketch, "E85", {"center": v(-2.16, 104.38) * mm, "radius": 6 * mm});
            skLineSegment(sketch, "E86", {"start": v(-2.16, 104.38) * mm, "end": v(-2.16, 74.38) * mm, "construction": true});
            skLineSegment(sketch, "E87", {"start": v(-74.53, 0) * mm, "end": v(73.98, 0) * mm, "construction": true});
            skLineSegment(sketch, "E88.MirrorCS", {"start": v(-31.53, -74.38) * mm, "end": v(-17.16, -92.38) * mm});
            skLineSegment(sketch, "E89.MirrorCS", {"start": v(-17.16, -92.38) * mm, "end": v(-17.16, -104.38) * mm});
            skArc(sketch, "E90.MirrorCS", {"start": v(12.84, -104.38) * mm, "mid": v(-2.16, -119.38) * mm, "end": v(-17.16, -104.38) * mm});
            skLineSegment(sketch, "E91.MirrorCS", {"start": v(12.84, -92.38) * mm, "end": v(12.84, -104.38) * mm});
            skLineSegment(sketch, "E92.MirrorCS", {"start": v(30.84, -74.38) * mm, "end": v(12.84, -92.38) * mm});
            skLineSegment(sketch, "E93.MirrorCS", {"start": v(-31.53, -74.38) * mm, "end": v(30.84, -74.38) * mm});
            skLineSegment(sketch, "E94.MirrorCS", {"start": v(-2.16, -104.38) * mm, "end": v(-2.16, -74.38) * mm, "construction": true});
            skCircle(sketch, "E95.MirrorC", {"center": v(-2.16, -104.38) * mm, "radius": 6 * mm});
            skSolve(sketch);
        }
        {
            var Q0;
            Q0 = qSketchRegion(id + "F16", true);
            extrude(context, id + "F17", {"entities" : qUnion([Q0]), "depth" : 25 * mm});
        }
    });
